# Revit family: Fioriera RING
name_source: partatom
category: Modelli generici
revit_build: Autodesk Revit 2018 (Build: 20170223_1515(x64)
units: mm (PartAtom-declared; Revit-internal decimal feet)

## family parameters
Basato su piano di lavoro = No
Condiviso = No
Punto di calcolo locali = No
Può ospitare armatura = No
Quota connettore circolare = Usa diametro
Sempre verticale = Sì
Taglio con vuoti quando caricato = No
Tipo di parte = Normale

## types (3) — shared parameters
Accessori = Contenitore interno in acciaio zincato
Accessories = Inner container in galvanized steel
BIM Name = RING - 400 Lt.
BIM Object Type = FIORIERE - PLANTERS
Code = 0FIAR014
Descrizione Tecnica Famiglia = fioriera circolare mod. “RING”, costituita da una fioriera monolitica dotata di foro passante centrale per la predisposizione non solo di fiori ma anche di piante con fusto.
Designer = BELLITALIA DESIGN
Dimensions = Ø=1575 mm R=786 mm r=446 mm h=480 mm
Family Name = RING
Fissaggio = Appoggio
Fixings = Freestanding
IFC = Furniture and Furnishings
MASTERFORMAT 2014 (DESCRIPTION/CODE) = Planters / 32 94 33
OMNICLASS (DESCRIPTION/CODE) = Planters / 23-11 27 13 17
Technical Description Family = circular planter mod. “RING”, consisting of a planter monolithic with a central through hole for the set not only of flowers but also of plants confused.
UNICLASS 1.4 (DESCRIPTION/CODE) = Planters / L8721
UNICLASS 2.0 (DESCRIPTION/CODE) = Herb Planters / Pr 45 63 63 337
UNIFORMAT II (DESCRIPTION/CODE) = Furnishings / E20
UNSPSC CATEGORY (CODE) = Furnishings / E20
URL Eng = https://www.bellitalia.net
URL Ita = https://www.bellitalia.net
Weight ( kg) = 963 Kg.

## per-type parameters (varying)
| type | Descrizione Tecnica per Codice | MATERIALE FIORIERA | Materiale Principale | Materiale Secondario | Primary Material | Secondary Material | Technical Description for Article |
| 0FIAR014 - GRANITO - 400 Lt | FIORIERA AD ANELLO IN GRANITO (COLORE A SCELTA) LUCIDO ANTIDECADIMENTO | GRANITO | Granito Bianco | Pietre di Granito | White Granite | Reconstituted Granite | RING PLANTER IN GRANITO (COLOR TO BE CHOSEN) POLISHED ANTI-DECAY 
VARNISH |
| 0FIAR014 - PIETRE PREZIOSE - 400 Lt | FIORIERA AD ANELLO IN PIETRE PREZIOSE (COLORE DA SCELTA TRANNE VERDE
ALPS) VERNICE ANTIDECADIMENTO LUCIDA | PIETRE PREZIOSE | Pietre Preziose Ricostituite Bianco Carrara | Pietre Preziose Ricostituite | White Carrara Reconstituted Gemstones | Reconstituted Precious Stone | RING PLANTER IN PRECIOUS STONES (COLOR TO BE CHOSEN EXCEPT GREEN 
ALPS) POLISHED ANTI-DECAY VARNISH |
| 0FIAR014 - VERDE ALPI - 400 Lt | FIORIERA AD ANELLO VERDE ALPI VERNICE LUCIDA ANTI-CARREGGIAMENTO | VERDE ALPI | Pietre Preziose Ricostituite Verde Alpi | Pietre Preziose Ricostituite | Green Alps Reconstituted Precious Stones | Reconstituted Precious Stone | RING PLANTER IN GREEN ALPS POLISHED ANTI-DECAY VARNISH |
